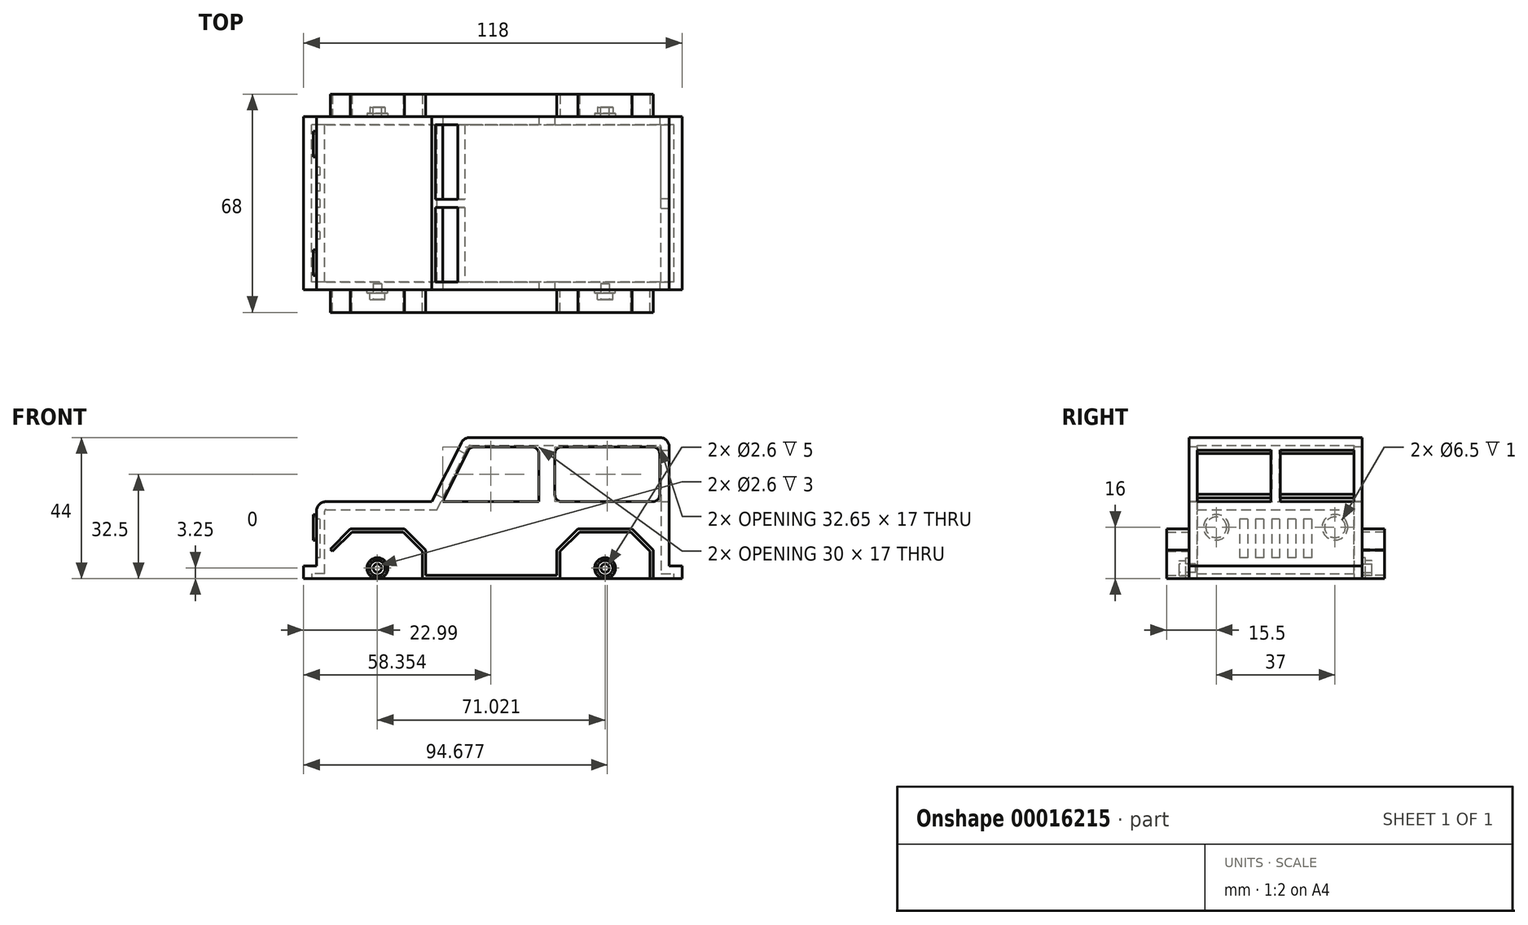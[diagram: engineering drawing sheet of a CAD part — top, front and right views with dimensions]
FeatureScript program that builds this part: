
annotation { "Feature Type Name" : "Feature", "Feature Type Description" : "" }
export const myFeature = defineFeature(function(context is Context, id is Id, definition is map)
    precondition{}
    {
        {
            var Q0;
            Q0=qCreatedBy(makeId("Front.planeOp"),FACE);
            var sketch = newSketch(context, id + "F0", { "sketchPlane" : qUnion([Q0])});
            skLineSegment(sketch, "E0", {"start": v(-54, 4) * mm, "end": v(-54, 21) * mm});
            skLineSegment(sketch, "E1", {"start": v(-51, 24) * mm, "end": v(-18, 24) * mm});
            skLineSegment(sketch, "E2", {"start": v(-18, 24) * mm, "end": v(-8.83, 42.34) * mm});
            skLineSegment(sketch, "E3", {"start": v(-6.15, 44) * mm, "end": v(53, 44) * mm});
            skLineSegment(sketch, "E4", {"start": v(56, 41) * mm, "end": v(56, 4) * mm});
            skLineSegment(sketch, "E5", {"start": v(56, 0) * mm, "end": v(-54, 0) * mm});
            skLineSegment(sketch, "E6", {"start": v(-36, 0) * mm, "end": v(36, 0) * mm, "construction": true});
            skCircle(sketch, "E7", {"center": v(-36, 0) * mm, "radius": 11.5 * mm, "construction": true});
            skCircle(sketch, "E8", {"center": v(36, 0) * mm, "radius": 11.5 * mm, "construction": true});
            skPoint(sketch, "E9.visualSharp", {"position": v(-54, 24) * mm});
            skArc(sketch, "E9.filletArc", {"start": v(-51, 24) * mm, "mid": v(-53.12, 23.12) * mm, "end": v(-54, 21) * mm});
            skPoint(sketch, "E10.visualSharp", {"position": v(-8, 44) * mm});
            skArc(sketch, "E10.filletArc", {"start": v(-6.15, 44) * mm, "mid": v(-7.72, 43.55) * mm, "end": v(-8.83, 42.34) * mm});
            skPoint(sketch, "E11.visualSharp", {"position": v(56, 44) * mm});
            skArc(sketch, "E11.filletArc", {"start": v(56, 41) * mm, "mid": v(55.12, 43.12) * mm, "end": v(53, 44) * mm});
            skPoint(sketch, "E12.visualSharp", {"position": v(56, 0) * mm});
            skLineSegment(sketch, "E13.bottom", {"start": v(-54, 4) * mm, "end": v(-58, 4) * mm});
            skLineSegment(sketch, "E13.top", {"start": v(-54, 0) * mm, "end": v(-58, 0) * mm});
            skLineSegment(sketch, "E13.right", {"start": v(-58, 4) * mm, "end": v(-58, 0) * mm});
            skLineSegment(sketch, "E14.bottom", {"start": v(56, 0) * mm, "end": v(60, 0) * mm});
            skLineSegment(sketch, "E14.top", {"start": v(56, 4) * mm, "end": v(60, 4) * mm});
            skLineSegment(sketch, "E14.right", {"start": v(60, 0) * mm, "end": v(60, 4) * mm});
            skSolve(sketch);
        }
        {
            var Q0;
            Q0=qSketchRegion(id+"F0",true);
            extrude(context, id + "F1", {"entities" : qUnion([Q0]), "depth" : 27 * mm, "hasSecondDirection" : true, "secondDirectionOppositeDirection" : true, "secondDirectionDepth" : 27 * mm});
        }
        {
            var Q0;
            Q0=makeQuery(id+"F1.opExtrude","SWEPT_FACE",FACE,{"disambiguationData":[OSD([sQuery(id+"F0.wireOp",EDGE,"E5")])]});
            shell(context, id + "F2", {"entities" : qUnion([Q0]), "thickness" : 2.5 * mm});
        }
        {
            var Q0;
            Q0=makeQuery(id+"F1.opExtrude","SWEPT_FACE",FACE,{"disambiguationData":[OSD([sQuery(id+"F0.wireOp",EDGE,"E2")])]});
            var sketch = newSketch(context, id + "F3", { "sketchPlane" : qUnion([Q0])});
            skLineSegment(sketch, "E15.0", {"start": v(-24.5, 31.42) * mm, "end": v(-24.5, 15.92) * mm});
            skLineSegment(sketch, "E15.1", {"start": v(24.5, 31.42) * mm, "end": v(1.25, 31.42) * mm});
            skLineSegment(sketch, "E15.2", {"start": v(24.5, 15.92) * mm, "end": v(24.5, 31.42) * mm});
            skLineSegment(sketch, "E15.3", {"start": v(-24.5, 15.92) * mm, "end": v(-1.25, 15.92) * mm});
            skLineSegment(sketch, "E16.top", {"start": v(-1.25, 15.92) * mm, "end": v(1.25, 15.92) * mm});
            skLineSegment(sketch, "E16.left", {"start": v(-1.25, 31.42) * mm, "end": v(-1.25, 15.92) * mm});
            skLineSegment(sketch, "E16.right", {"start": v(1.25, 31.42) * mm, "end": v(1.25, 15.92) * mm});
            skLineSegment(sketch, "E17.trimOffspring", {"start": v(1.25, 15.92) * mm, "end": v(24.5, 15.92) * mm});
            skLineSegment(sketch, "E18.trimOffspring", {"start": v(-1.25, 31.42) * mm, "end": v(-24.5, 31.42) * mm});
            skSolve(sketch);
        }
        {
            var Q0;
            Q0=qSketchRegion(id+"F3",true);
            extrude(context, id + "F4", {"entities" : qUnion([Q0]), "operationType" : NewBodyOperationType.REMOVE, "endBound" : BoundingType.UP_TO_NEXT, "oppositeDirection" : true, "depth" : 25 * mm});
        }
        {
            var Q0;
            Q0=makeQuery(id+"F1.opExtrude","CAP_FACE",FACE,{"disambiguationData":[OSD([sQuery(id+"F0.wireOp",EDGE,"E0"),sQuery(id+"F0.wireOp",EDGE,"E1"),sQuery(id+"F0.wireOp",EDGE,"E2"),sQuery(id+"F0.wireOp",EDGE,"E3"),sQuery(id+"F0.wireOp",EDGE,"E4"),sQuery(id+"F0.wireOp",EDGE,"E5"),sQuery(id+"F0.wireOp",EDGE,"E9.filletArc"),sQuery(id+"F0.wireOp",EDGE,"E10.filletArc"),sQuery(id+"F0.wireOp",EDGE,"E11.filletArc"),sQuery(id+"F0.wireOp",EDGE,"E13.bottom"),sQuery(id+"F0.wireOp",EDGE,"E13.top"),sQuery(id+"F0.wireOp",EDGE,"E13.right"),sQuery(id+"F0.wireOp",EDGE,"E14.bottom"),sQuery(id+"F0.wireOp",EDGE,"E14.top"),sQuery(id+"F0.wireOp",EDGE,"E14.right")])],"isStart":false});
            var sketch = newSketch(context, id + "F5", { "sketchPlane" : qUnion([Q0])});
            skLineSegment(sketch, "E19", {"start": v(-14.65, 24) * mm, "end": v(-6.7, 39.9) * mm});
            skLineSegment(sketch, "E20", {"start": v(-4.9, 41) * mm, "end": v(13.35, 41) * mm});
            skLineSegment(sketch, "E21", {"start": v(15.35, 39) * mm, "end": v(15.35, 24) * mm});
            skLineSegment(sketch, "E22", {"start": v(15.35, 24) * mm, "end": v(-14.65, 24) * mm});
            skLineSegment(sketch, "E23.bottom", {"start": v(22.35, 41) * mm, "end": v(51, 41) * mm});
            skLineSegment(sketch, "E23.top", {"start": v(22.35, 24) * mm, "end": v(51, 24) * mm});
            skLineSegment(sketch, "E23.left", {"start": v(20.35, 39) * mm, "end": v(20.35, 26) * mm});
            skLineSegment(sketch, "E23.right", {"start": v(53, 39) * mm, "end": v(53, 26) * mm});
            skPoint(sketch, "E24.visualSharp", {"position": v(-6.15, 41) * mm});
            skArc(sketch, "E24.filletArc", {"start": v(-4.9, 41) * mm, "mid": v(-5.96, 40.7) * mm, "end": v(-6.7, 39.9) * mm});
            skPoint(sketch, "E25.visualSharp", {"position": v(20.35, 41) * mm});
            skArc(sketch, "E25.filletArc", {"start": v(22.35, 41) * mm, "mid": v(20.94, 40.41) * mm, "end": v(20.35, 39) * mm});
            skPoint(sketch, "E26.visualSharp", {"position": v(53, 41) * mm});
            skArc(sketch, "E26.filletArc", {"start": v(53, 39) * mm, "mid": v(52.41, 40.41) * mm, "end": v(51, 41) * mm});
            skPoint(sketch, "E27.visualSharp", {"position": v(53, 24) * mm});
            skArc(sketch, "E27.filletArc", {"start": v(51, 24) * mm, "mid": v(52.41, 24.59) * mm, "end": v(53, 26) * mm});
            skPoint(sketch, "E28.visualSharp", {"position": v(20.35, 24) * mm});
            skArc(sketch, "E28.filletArc", {"start": v(20.35, 26) * mm, "mid": v(20.94, 24.59) * mm, "end": v(22.35, 24) * mm});
            skPoint(sketch, "E29.visualSharp", {"position": v(15.35, 41) * mm});
            skArc(sketch, "E29.filletArc", {"start": v(15.35, 39) * mm, "mid": v(14.77, 40.41) * mm, "end": v(13.35, 41) * mm});
            skSolve(sketch);
        }
        {
            var Q0;
            Q0=qSketchRegion(id+"F5",true);
            extrude(context, id + "F6", {"entities" : qUnion([Q0]), "operationType" : NewBodyOperationType.REMOVE, "endBound" : BoundingType.THROUGH_ALL, "oppositeDirection" : true, "depth" : 25 * mm});
        }
        {
            var Q0;
            Q0=makeQuery(id+"F1.opExtrude","SWEPT_FACE",FACE,{"disambiguationData":[OSD([sQuery(id+"F0.wireOp",EDGE,"E4")])]});
            var sketch = newSketch(context, id + "F7", { "sketchPlane" : qUnion([Q0])});
            skLineSegment(sketch, "E30.bottom", {"start": v(24.5, 24) * mm, "end": v(1.5, 24) * mm});
            skLineSegment(sketch, "E30.top", {"start": v(24.5, 40) * mm, "end": v(1.5, 40) * mm});
            skLineSegment(sketch, "E30.left", {"start": v(24.5, 24) * mm, "end": v(24.5, 40) * mm});
            skLineSegment(sketch, "E30.right", {"start": v(1.5, 24) * mm, "end": v(1.5, 40) * mm});
            skLineSegment(sketch, "E31.bottom", {"start": v(-1.5, 24) * mm, "end": v(-24.5, 24) * mm});
            skLineSegment(sketch, "E31.top", {"start": v(-1.5, 40) * mm, "end": v(-24.5, 40) * mm});
            skLineSegment(sketch, "E31.left", {"start": v(-1.5, 24) * mm, "end": v(-1.5, 40) * mm});
            skLineSegment(sketch, "E31.right", {"start": v(-24.5, 24) * mm, "end": v(-24.5, 40) * mm});
            skSolve(sketch);
        }
        {
            var Q0;
            Q0=makeQuery(id+"F1.opExtrude","SWEPT_FACE",FACE,{"disambiguationData":[OSD([sQuery(id+"F0.wireOp",EDGE,"E0")])]});
            var sketch = newSketch(context, id + "F8", { "sketchPlane" : qUnion([Q0])});
            skCircle(sketch, "E32", {"center": v(-18.5, 16) * mm, "radius": 4 * mm});
            skCircle(sketch, "E33", {"center": v(18.5, 16) * mm, "radius": 4 * mm});
            skCircle(sketch, "E34", {"center": v(-18.5, 16) * mm, "radius": 3.25 * mm});
            skCircle(sketch, "E35", {"center": v(18.5, 16) * mm, "radius": 3.25 * mm});
            skSolve(sketch);
        }
        {
            var Q0;
            Q0=qSketchRegion(id+"F7",true);
            extrude(context, id + "F9", {"entities" : qUnion([Q0]), "operationType" : NewBodyOperationType.REMOVE, "endBound" : BoundingType.UP_TO_NEXT, "oppositeDirection" : true, "depth" : 25 * mm});
        }
        {
            var Q0;
            Q0=qSketchRegion(id+"F8",true);
            extrude(context, id + "F10", {"entities" : qUnion([Q0]), "operationType" : NewBodyOperationType.ADD, "depth" : 1 * mm});
        }
        {
            var Q0;
            Q0=makeQuery(id+"F1.opExtrude","CAP_FACE",FACE,{"disambiguationData":[OSD([sQuery(id+"F0.wireOp",EDGE,"E0"),sQuery(id+"F0.wireOp",EDGE,"E1"),sQuery(id+"F0.wireOp",EDGE,"E2"),sQuery(id+"F0.wireOp",EDGE,"E3"),sQuery(id+"F0.wireOp",EDGE,"E4"),sQuery(id+"F0.wireOp",EDGE,"E5"),sQuery(id+"F0.wireOp",EDGE,"E9.filletArc"),sQuery(id+"F0.wireOp",EDGE,"E10.filletArc"),sQuery(id+"F0.wireOp",EDGE,"E11.filletArc"),sQuery(id+"F0.wireOp",EDGE,"E13.bottom"),sQuery(id+"F0.wireOp",EDGE,"E13.top"),sQuery(id+"F0.wireOp",EDGE,"E13.right"),sQuery(id+"F0.wireOp",EDGE,"E14.bottom"),sQuery(id+"F0.wireOp",EDGE,"E14.top"),sQuery(id+"F0.wireOp",EDGE,"E14.right")])],"isStart":false});
            var sketch = newSketch(context, id + "F11", { "sketchPlane" : qUnion([Q0])});
            skLineSegment(sketch, "E36", {"start": v(-49.02, 8.5) * mm, "end": v(-43.01, 14.51) * mm});
            skLineSegment(sketch, "E37", {"start": v(-43.01, 14.51) * mm, "end": v(-27.01, 14.51) * mm});
            skLineSegment(sketch, "E38", {"start": v(-27.01, 14.51) * mm, "end": v(-21, 8.5) * mm});
            skLineSegment(sketch, "E39", {"start": v(-21, 8.5) * mm, "end": v(-21, 0) * mm});
            skLineSegment(sketch, "E40", {"start": v(-21, 0) * mm, "end": v(22, 0) * mm});
            skLineSegment(sketch, "E41", {"start": v(22, 0) * mm, "end": v(22, 8.5) * mm});
            skLineSegment(sketch, "E42", {"start": v(22, 8.5) * mm, "end": v(28.01, 14.51) * mm});
            skLineSegment(sketch, "E43", {"start": v(28.01, 14.51) * mm, "end": v(44.01, 14.51) * mm});
            skLineSegment(sketch, "E44", {"start": v(44.01, 14.51) * mm, "end": v(50.02, 8.5) * mm});
            skLineSegment(sketch, "E45", {"start": v(50.02, 8.5) * mm, "end": v(50.02, 0) * mm});
            skLineSegment(sketch, "E46.0", {"start": v(51.02, 8.91) * mm, "end": v(51.02, 0) * mm});
            skLineSegment(sketch, "E46.1", {"start": v(44.42, 15.51) * mm, "end": v(51.02, 8.91) * mm});
            skLineSegment(sketch, "E46.2", {"start": v(27.6, 15.51) * mm, "end": v(44.42, 15.51) * mm});
            skLineSegment(sketch, "E46.3", {"start": v(21, 8.91) * mm, "end": v(27.6, 15.51) * mm});
            skLineSegment(sketch, "E46.4", {"start": v(21, 1) * mm, "end": v(21, 8.91) * mm});
            skLineSegment(sketch, "E46.5", {"start": v(-20, 1) * mm, "end": v(21, 1) * mm});
            skLineSegment(sketch, "E46.6", {"start": v(-20, 8.91) * mm, "end": v(-20, 1) * mm});
            skLineSegment(sketch, "E46.7", {"start": v(-26.6, 15.51) * mm, "end": v(-20, 8.91) * mm});
            skLineSegment(sketch, "E46.8", {"start": v(-43.42, 15.51) * mm, "end": v(-26.6, 15.51) * mm});
            skLineSegment(sketch, "E46.9", {"start": v(-49.73, 9.2) * mm, "end": v(-43.42, 15.51) * mm});
            skLineSegment(sketch, "E47", {"start": v(-49.73, 9.2) * mm, "end": v(-49.02, 8.5) * mm});
            skLineSegment(sketch, "E48", {"start": v(50.02, 0) * mm, "end": v(51.02, 0) * mm});
            skSolve(sketch);
        }
        {
            var Q0;
            Q0=qSketchRegion(id+"F11",true);
            var Q1;
            Q1=qConstructionFilter(qBodyType(qCreatedBy(id+"F11",EDGE),BodyType.WIRE),ConstructionObject.NO);
            extrude(context, id + "F12", {"entities" : qUnion([Q0]), "surfaceEntities" : qUnion([Q1]), "depth" : 7 * mm});
        }
        {
            var Q0;
            Q0=makeQuery(id+"F12.opExtrude","SWEPT_BODY",BODY,{"disambiguationData":[OSD([sQuery(id+"F11.wireOp",EDGE,"E36"),sQuery(id+"F11.wireOp",EDGE,"E37"),sQuery(id+"F11.wireOp",EDGE,"E38"),sQuery(id+"F11.wireOp",EDGE,"E39"),sQuery(id+"F11.wireOp",EDGE,"E40"),sQuery(id+"F11.wireOp",EDGE,"E41"),sQuery(id+"F11.wireOp",EDGE,"E42"),sQuery(id+"F11.wireOp",EDGE,"E43"),sQuery(id+"F11.wireOp",EDGE,"E44"),sQuery(id+"F11.wireOp",EDGE,"E45"),sQuery(id+"F11.wireOp",EDGE,"E46.0"),sQuery(id+"F11.wireOp",EDGE,"E46.1"),sQuery(id+"F11.wireOp",EDGE,"E46.2"),sQuery(id+"F11.wireOp",EDGE,"E46.3"),sQuery(id+"F11.wireOp",EDGE,"E46.4"),sQuery(id+"F11.wireOp",EDGE,"E46.5"),sQuery(id+"F11.wireOp",EDGE,"E46.6"),sQuery(id+"F11.wireOp",EDGE,"E46.7"),sQuery(id+"F11.wireOp",EDGE,"E46.8"),sQuery(id+"F11.wireOp",EDGE,"E46.9"),sQuery(id+"F11.wireOp",EDGE,"E47"),sQuery(id+"F11.wireOp",EDGE,"E48")])]});
            var Q1;
            Q1=qCreatedBy(makeId("Front.planeOp"),FACE);
            mirror(context, id + "F13", {"operationType" : NewBodyOperationType.ADD, "entities" : qUnion([Q0]), "mirrorPlane" : qUnion([Q1])});
        }
        {
            var Q0;
            {var subQ0=sQuery(id+"F0.wireOp",EDGE,"E0");var subQ1=sQuery(id+"F0.wireOp",EDGE,"E1");var subQ2=sQuery(id+"F0.wireOp",EDGE,"E2");var subQ3=sQuery(id+"F0.wireOp",EDGE,"E3");var subQ4=sQuery(id+"F0.wireOp",EDGE,"E4");var subQ5=sQuery(id+"F0.wireOp",EDGE,"E5");var subQ6=sQuery(id+"F0.wireOp",EDGE,"E9.filletArc");var subQ7=sQuery(id+"F0.wireOp",EDGE,"E10.filletArc");var subQ8=sQuery(id+"F0.wireOp",EDGE,"E11.filletArc");var subQ9=sQuery(id+"F0.wireOp",EDGE,"E13.bottom");var subQ10=sQuery(id+"F0.wireOp",EDGE,"E13.top");var subQ11=sQuery(id+"F0.wireOp",EDGE,"E13.right");var subQ12=sQuery(id+"F0.wireOp",EDGE,"E14.bottom");var subQ13=sQuery(id+"F0.wireOp",EDGE,"E14.top");var subQ14=sQuery(id+"F0.wireOp",EDGE,"E14.right");Q0=makeQuery(id+"F13.boolean.opBoolean","SPLIT",FACE,{"disambiguationData":[TD([makeQuery(id+"F1.opExtrude","SWEPT_FACE",FACE,{"disambiguationData":[OSD([subQ0])]})])],"derivedFrom":makeQuery(id+"F1.opExtrude","CAP_FACE",FACE,{"disambiguationData":[OSD([subQ0,subQ1,subQ2,subQ3,subQ4,subQ5,subQ6,subQ7,subQ8,subQ9,subQ10,subQ11,subQ12,subQ13,subQ14])],"isStart":false})});}
            var sketch = newSketch(context, id + "F14", { "sketchPlane" : qUnion([Q0])});
            skCircle(sketch, "E49", {"center": v(-35.01, 3.25) * mm, "radius": 3.25 * mm});
            skCircle(sketch, "E50", {"center": v(36.01, 3.25) * mm, "radius": 3.25 * mm});
            skLineSegment(sketch, "E51", {"start": v(-35.01, 3.25) * mm, "end": v(-35.01, 14.51) * mm, "construction": true});
            skLineSegment(sketch, "E52", {"start": v(36.01, 3.25) * mm, "end": v(36.01, 14.51) * mm, "construction": true});
            skSolve(sketch);
        }
        {
            var Q0;
            Q0=qSketchRegion(id+"F14",true);
            extrude(context, id + "F15", {"entities" : qUnion([Q0]), "depth" : 1 * mm});
        }
        {
            var Q0;
            Q0=makeQuery(id+"F15.opExtrude","CAP_FACE",FACE,{"disambiguationData":[OSD([sQuery(id+"F14.wireOp",EDGE,"E49")])],"isStart":false});
            var sketch = newSketch(context, id + "F16", { "sketchPlane" : qUnion([Q0])});
            skCircle(sketch, "E53", {"center": v(-35.01, 3.25) * mm, "radius": 2.4 * mm});
            skCircle(sketch, "E54", {"center": v(36.01, 3.25) * mm, "radius": 2.4 * mm});
            skSolve(sketch);
        }
        {
            var Q0;
            Q0=qSketchRegion(id+"F16",true);
            extrude(context, id + "F17", {"entities" : qUnion([Q0]), "operationType" : NewBodyOperationType.ADD, "depth" : 2 * mm});
        }
        {
            var Q0;
            Q0=makeQuery(id+"F17.opExtrude","CAP_FACE",FACE,{"disambiguationData":[OSD([sQuery(id+"F16.wireOp",EDGE,"E53")])],"isStart":false});
            var sketch = newSketch(context, id + "F18", { "sketchPlane" : qUnion([Q0])});
            skCircle(sketch, "E55", {"center": v(-35.01, 3.25) * mm, "radius": 1.3 * mm});
            skCircle(sketch, "E56", {"center": v(36.01, 3.25) * mm, "radius": 1.3 * mm});
            skSolve(sketch);
        }
        {
            var Q0;
            Q0=qSketchRegion(id+"F18",true);
            extrude(context, id + "F19", {"entities" : qUnion([Q0]), "operationType" : NewBodyOperationType.REMOVE, "oppositeDirection" : true, "depth" : 5 * mm});
        }
        {
            var Q0;
            Q0=makeQuery(id+"F15.opExtrude","SWEPT_BODY",BODY,{"disambiguationData":[OSD([sQuery(id+"F14.wireOp",EDGE,"E50")])]});
            var Q1;
            Q1=makeQuery(id+"F15.opExtrude","SWEPT_BODY",BODY,{"disambiguationData":[OSD([sQuery(id+"F14.wireOp",EDGE,"E49")])]});
            var Q2;
            Q2=qCreatedBy(makeId("Front.planeOp"),FACE);
            mirror(context, id + "F20", {"operationType" : NewBodyOperationType.ADD, "entities" : qUnion([Q0, Q1]), "mirrorPlane" : qUnion([Q2])});
        }
        {
            var Q0;
            {var subQ0=sQuery(id+"F0.wireOp",EDGE,"E0");var subQ2=sQuery(id+"F0.wireOp",EDGE,"E9.filletArc");Q0=makeQuery(id+"F10.boolean.opBoolean","SPLIT",FACE,{"disambiguationData":[TD([makeQuery(id+"F1.opExtrude","SWEPT_FACE",FACE,{"disambiguationData":[OSD([subQ2])]})])],"derivedFrom":makeQuery(id+"F1.opExtrude","SWEPT_FACE",FACE,{"disambiguationData":[OSD([subQ0])]})});}
            var sketch = newSketch(context, id + "F21", { "sketchPlane" : qUnion([Q0])});
            skLineSegment(sketch, "E57.bottom", {"start": v(-11.25, 18.5) * mm, "end": v(-8.75, 18.5) * mm});
            skLineSegment(sketch, "E57.top", {"start": v(-11.25, 6.5) * mm, "end": v(-8.75, 6.5) * mm});
            skLineSegment(sketch, "E57.left", {"start": v(-11.25, 18.5) * mm, "end": v(-11.25, 6.5) * mm});
            skLineSegment(sketch, "E57.right", {"start": v(-8.75, 18.5) * mm, "end": v(-8.75, 6.5) * mm});
            skLineSegment(sketch, "E58.bottom", {"start": v(-6.25, 18.5) * mm, "end": v(-3.75, 18.5) * mm});
            skLineSegment(sketch, "E58.top", {"start": v(-6.25, 6.5) * mm, "end": v(-3.75, 6.5) * mm});
            skLineSegment(sketch, "E58.left", {"start": v(-6.25, 18.5) * mm, "end": v(-6.25, 6.5) * mm});
            skLineSegment(sketch, "E58.right", {"start": v(-3.75, 18.5) * mm, "end": v(-3.75, 6.5) * mm});
            skLineSegment(sketch, "E59.bottom", {"start": v(3.75, 18.5) * mm, "end": v(6.25, 18.5) * mm});
            skLineSegment(sketch, "E59.top", {"start": v(3.75, 6.5) * mm, "end": v(6.25, 6.5) * mm});
            skLineSegment(sketch, "E59.left", {"start": v(3.75, 18.5) * mm, "end": v(3.75, 6.5) * mm});
            skLineSegment(sketch, "E59.right", {"start": v(6.25, 18.5) * mm, "end": v(6.25, 6.5) * mm});
            skLineSegment(sketch, "E60.bottom", {"start": v(8.75, 18.5) * mm, "end": v(11.25, 18.5) * mm});
            skLineSegment(sketch, "E60.top", {"start": v(8.75, 6.5) * mm, "end": v(11.25, 6.5) * mm});
            skLineSegment(sketch, "E60.left", {"start": v(8.75, 18.5) * mm, "end": v(8.75, 6.5) * mm});
            skLineSegment(sketch, "E60.right", {"start": v(11.25, 18.5) * mm, "end": v(11.25, 6.5) * mm});
            skLineSegment(sketch, "E61.left", {"start": v(-1.25, 18.5) * mm, "end": v(-1.25, 6.5) * mm});
            skLineSegment(sketch, "E61.top", {"start": v(-1.25, 6.5) * mm, "end": v(1.25, 6.5) * mm});
            skLineSegment(sketch, "E61.bottom", {"start": v(-1.25, 18.5) * mm, "end": v(1.25, 18.5) * mm});
            skLineSegment(sketch, "E61.right", {"start": v(1.25, 18.5) * mm, "end": v(1.25, 6.5) * mm});
            skLineSegment(sketch, "E62", {"start": v(-8.75, 6.5) * mm, "end": v(-6.25, 6.5) * mm, "construction": true});
            skLineSegment(sketch, "E63", {"start": v(-3.75, 6.5) * mm, "end": v(-1.25, 6.5) * mm, "construction": true});
            skLineSegment(sketch, "E64", {"start": v(1.25, 6.5) * mm, "end": v(3.75, 6.5) * mm, "construction": true});
            skLineSegment(sketch, "E65", {"start": v(6.25, 6.5) * mm, "end": v(8.75, 6.5) * mm, "construction": true});
            skSolve(sketch);
        }
        {
            var Q0;
            Q0=qSketchRegion(id+"F21",true);
            extrude(context, id + "F22", {"entities" : qUnion([Q0]), "operationType" : NewBodyOperationType.REMOVE, "oppositeDirection" : true, "depth" : 1 * mm});
        }
    });
